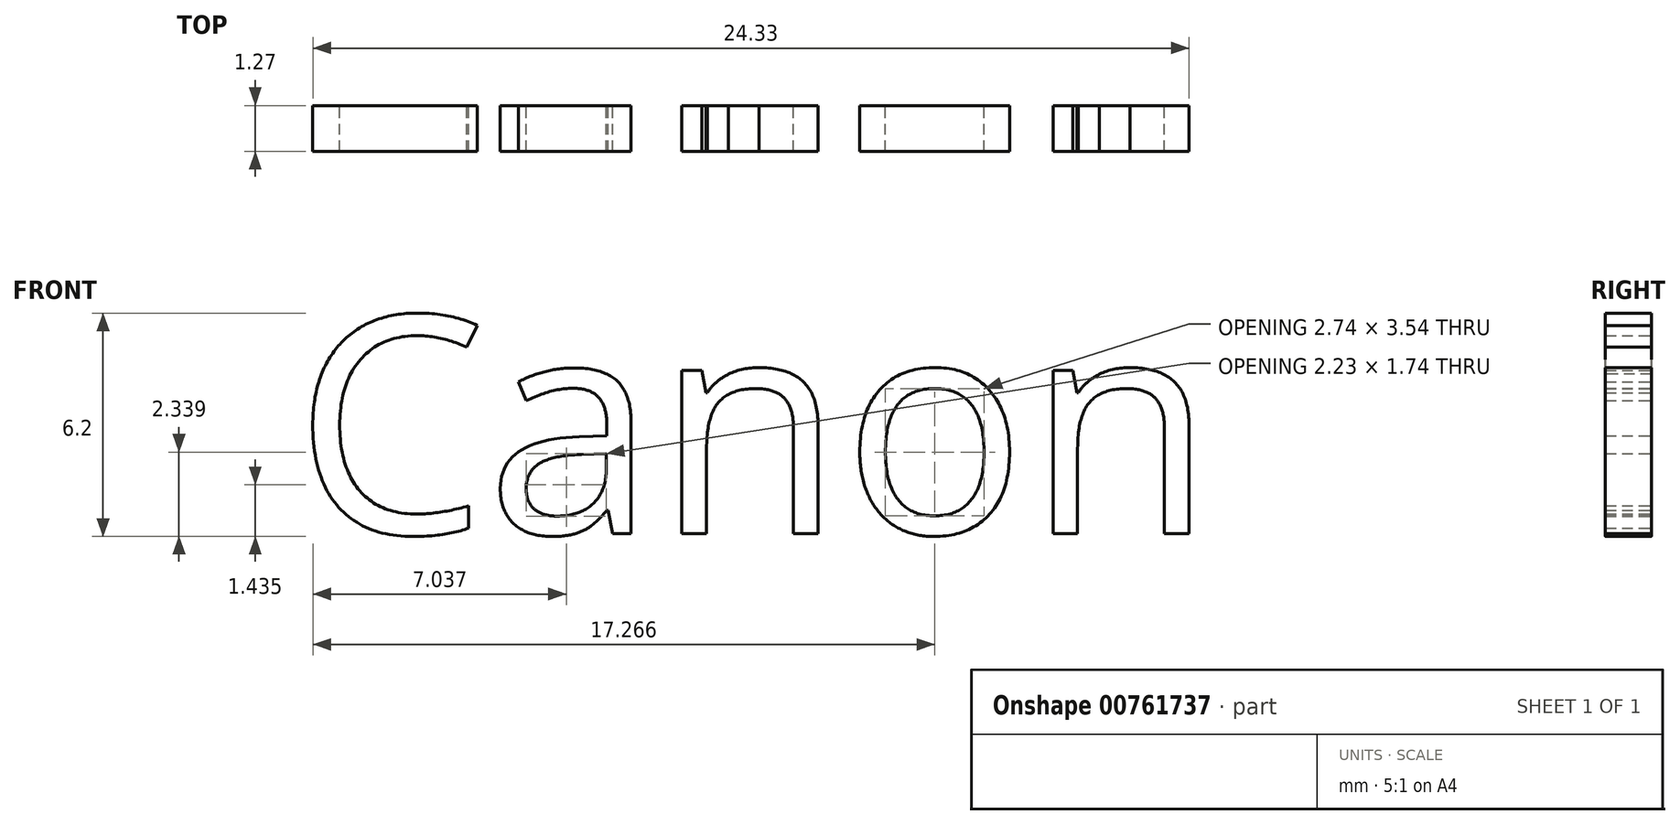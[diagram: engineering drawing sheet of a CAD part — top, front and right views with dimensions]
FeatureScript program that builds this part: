
annotation { "Feature Type Name" : "Feature", "Feature Type Description" : "" }
export const myFeature = defineFeature(function(context is Context, id is Id, definition is map)
    precondition{}
    {
        {
            var Q0;
            Q0=qCreatedBy(makeId("Front.planeOp"),FACE);
            var sketch = newSketch(context, id + "F0", { "sketchPlane" : qUnion([Q0])});
            skText(sketch, "E0", { "text": "Canon\n", "fontName": "OpenSans-Regular.ttf"});
            const initialGuessF0  = {"E0": [-0.01844, 0.0093, 1, 0, 0.00609]};
            skSetInitialGuess(sketch, initialGuessF0);
            skSolve(sketch);
        }
        {
            var Q0;
            Q0 = qSketchRegion(id + "F0", true);
            extrude(context, id + "F1", {"entities" : qUnion([Q0]), "depth" : 1.27 * mm, "offsetDistance" : 25.4 * mm});
        }
    });
